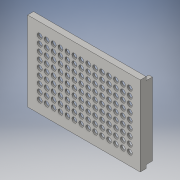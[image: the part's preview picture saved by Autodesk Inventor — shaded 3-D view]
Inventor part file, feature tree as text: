
AUTODESK INVENTOR PART (.ipt)
format: ipt  version: 2016 (Build 200138000, 138)  size: 313,856 bytes
history: native  units: mm
features: sketch x4, extrude x3
ambient origin geometry x8: Origin, YZ Plane, XZ Plane, XY Plane, X Axis, Y Axis, Z Axis, Center Point
bodies: Solid1 (feature_tree)
feature tree (7):
  extrude  "Extrusion1"  Depth=63.0mm
  extrude  "Extrusion2"  Depth=7.5mm
  sketch  "Sketch5"  dims[d4=7.5mm d5=4.3mm]
  extrude  "Extrusion3"  Depth=4.3mm
  sketch  "Sketch1"  dims[d0=91.5mm d1=63.0mm]
  sketch  "Sketch2"  dims[d2=4.3mm d3=7.5mm]
  sketch  "Sketch6"  dims[d6=6.0mm d7=4.3mm d8=6.0mm d9=4.3mm d10=6.0mm d11=4.3mm d12=6.0mm d15=6.0mm d17=3.0mm d18=3.0mm d19=1.5mm d20=0.0mm d24=3.612mm d25=0.0mm d26=1.5mm d27=0.0mm d30=97.5mm d31=69.0mm d32=97.5mm d33=5.388mm d34=0.0mm]
